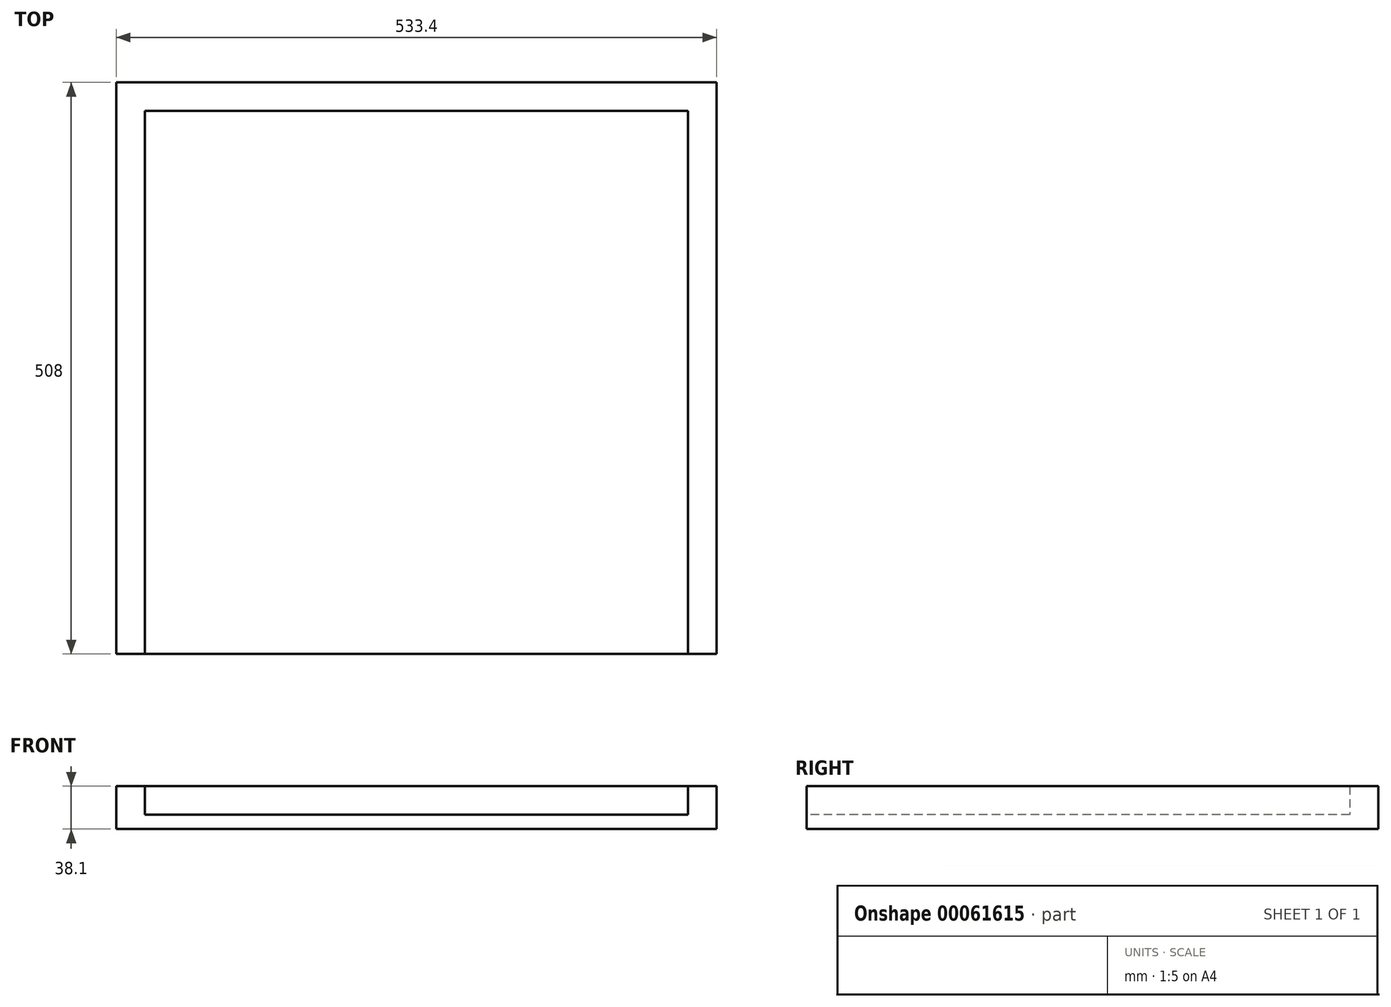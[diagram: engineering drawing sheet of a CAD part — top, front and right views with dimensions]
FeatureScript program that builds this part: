
annotation { "Feature Type Name" : "Feature", "Feature Type Description" : "" }
export const myFeature = defineFeature(function(context is Context, id is Id, definition is map)
    precondition{}
    {
        {
            var Q0;
            Q0=qCreatedBy(makeId("Top.planeOp"),FACE);
            var sketch = newSketch(context, id + "F0", { "sketchPlane" : qUnion([Q0])});
            skLineSegment(sketch, "E0.rect.bottom", {"start": v(-266.7, 254) * mm, "end": v(266.7, 254) * mm});
            skLineSegment(sketch, "E0.rect.top", {"start": v(-266.7, -254) * mm, "end": v(266.7, -254) * mm});
            skLineSegment(sketch, "E0.rect.left", {"start": v(-266.7, 254) * mm, "end": v(-266.7, -254) * mm});
            skLineSegment(sketch, "E0.rect.right", {"start": v(266.7, 254) * mm, "end": v(266.7, -254) * mm});
            skPoint(sketch, "E0.rect.middle", {"position": v(0, 0) * mm});
            skLineSegment(sketch, "E1.bottom", {"start": v(-266.7, 254) * mm, "end": v(-241.3, 254) * mm});
            skLineSegment(sketch, "E2.bottom", {"start": v(-241.3, 254) * mm, "end": v(241.3, 254) * mm});
            skSolve(sketch);
        }
        {
            var Q0;
            Q0=makeQuery(id+"F0.imprint","IMPRINT",FACE,{"disambiguationData":[TD([[makeQuery(id+"F0.imprint","IMPRINT",EDGE,{"derivedFrom":sQuery(id+"F0.wireOp",EDGE,"E0.rect.bottom")}),-1.0]])]});
            extrude(context, id + "F1", {"entities" : qUnion([Q0]), "depth" : 12.7 * mm});
        }
        {
            var Q0;
            Q0=makeQuery(id+"F1.opExtrude","CAP_FACE",FACE,{"disambiguationData":[OSD([sQuery(id+"F0.wireOp",EDGE,"E0.rect.bottom"),sQuery(id+"F0.wireOp",EDGE,"E0.rect.top"),sQuery(id+"F0.wireOp",EDGE,"E0.rect.left"),sQuery(id+"F0.wireOp",EDGE,"E0.rect.right"),sQuery(id+"F0.wireOp",EDGE,"E1.bottom"),sQuery(id+"F0.wireOp",EDGE,"E2.bottom")])],"isStart":false});
            var sketch = newSketch(context, id + "F2", { "sketchPlane" : qUnion([Q0])});
            skLineSegment(sketch, "E3.bottom", {"start": v(-266.7, 254) * mm, "end": v(-241.3, 254) * mm});
            skLineSegment(sketch, "E3.top", {"start": v(-266.7, -254) * mm, "end": v(-241.3, -254) * mm});
            skLineSegment(sketch, "E3.left", {"start": v(-266.7, 254) * mm, "end": v(-266.7, -254) * mm});
            skLineSegment(sketch, "E3.right", {"start": v(-241.3, 254) * mm, "end": v(-241.3, -254) * mm});
            skLineSegment(sketch, "E4.bottom", {"start": v(266.7, -254) * mm, "end": v(241.3, -254) * mm});
            skLineSegment(sketch, "E4.top", {"start": v(266.7, 254) * mm, "end": v(241.3, 254) * mm});
            skLineSegment(sketch, "E4.left", {"start": v(266.7, -254) * mm, "end": v(266.7, 254) * mm});
            skLineSegment(sketch, "E4.right", {"start": v(241.3, -254) * mm, "end": v(241.3, 254) * mm});
            skLineSegment(sketch, "E5.bottom", {"start": v(241.3, 254) * mm, "end": v(-241.3, 254) * mm});
            skLineSegment(sketch, "E5.top", {"start": v(241.3, 228.6) * mm, "end": v(-241.3, 228.6) * mm});
            skLineSegment(sketch, "E5.left", {"start": v(241.3, 254) * mm, "end": v(241.3, 228.6) * mm});
            skLineSegment(sketch, "E5.right", {"start": v(-241.3, 254) * mm, "end": v(-241.3, 228.6) * mm});
            skSolve(sketch);
        }
        {
            var Q0;
            Q0=makeQuery(id+"F2.imprint","IMPRINT",FACE,{"disambiguationData":[TD([[makeQuery(id+"F2.imprint","IMPRINT",EDGE,{"derivedFrom":sQuery(id+"F2.wireOp",EDGE,"E5.bottom")}),-1.0]])]});
            var Q1;
            Q1=makeQuery(id+"F2.imprint","IMPRINT",FACE,{"disambiguationData":[TD([[makeQuery(id+"F2.imprint","IMPRINT",EDGE,{"derivedFrom":sQuery(id+"F2.wireOp",EDGE,"E3.bottom")}),-1.0]])]});
            var Q2;
            Q2=makeQuery(id+"F2.imprint","IMPRINT",FACE,{"disambiguationData":[TD([[makeQuery(id+"F2.imprint","IMPRINT",EDGE,{"derivedFrom":sQuery(id+"F2.wireOp",EDGE,"E4.bottom")}),1.0]])]});
            extrude(context, id + "F3", {"entities" : qUnion([Q0, Q1, Q2]), "operationType" : NewBodyOperationType.ADD, "depth" : 25.4 * mm});
        }
    });
